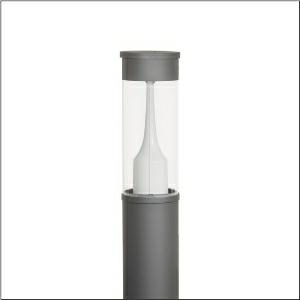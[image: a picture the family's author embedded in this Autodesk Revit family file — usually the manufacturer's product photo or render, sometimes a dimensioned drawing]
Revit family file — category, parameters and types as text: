
# Revit family: city-light_260_iq___st1_2a_5xa5295mf14h_84f0
name_source: partatom
category: Lighting Fixtures
units: mm (PartAtom-declared; Revit-internal decimal feet)

## family parameters
Cut with Voids When Loaded = No
Host = Face
Light Source = No
Part Type = Normal
Room Calculation Point = No
Round Connector Dimension = Use Diameter
Shared = No

## types (1)
- --- (1 x LED, 1540 lm, 11.8 W, 2700K)
    Apparent Load = 12 VA
    CIE Flux Codes = 22 61 93 96 100
    Color Rendering = 70
    Color Temperature = 2700K
    Default Elevation = 1800 mm
    Description = City-Light 260 iQ, light pillar, Module 540 iQ-SR, primary light control with 3 zone facetted reflector, of plastic, silver coated, highly specular, structured, primary optical cover: cover, of PMMA, transparent, partly coated, light distribution: ST1.2a, primary light characteristic: asymmetric, LED, High Power LED, rated luminous flux: 1.540lm, luminous efficacy: 131lm/W, light colour: 727, colour temperature: 2700K, control gear: ECG iQ, control: presetting dimming logarithmic, Street-Remote, Auto-Match, Temp-Guard, Lumen-Switch, Night-Set, Smart-Wire, Light-Fading, Desk-Remote (wireless, voltage-free reading and setting of iQ features in the workshop via application-optimized NFC function/RFID function), optimised constant luminous flux control (CLO 2.0), with terminal, 6-pole, max. 2.5mm², mains connection: 220..240V, AC, 50/60Hz, start of lifetime: 12W, end of lifetime: 12W, reduction: 6W, luminaire housing, cylindrical, of extruded aluminium section, coated, Siteco® metallic grey (DB 702S), length: 2.600mm, diameter: 200mm, Module 540 iQ-SR, traffic white (RAL 9016), equipment: standard, protection rating (complete): IP65, insulation class (complete): insulation class II (safety insulation), certification: CE, ENEC, VDE, packaging unit: 1 piece

Light Distribution: ST1.2a
    Height = 500 mm
    Lamp = 1 x LED
    Lamp Light Flux = 1540 lm
    Lamp Power = 11.8 W
    Lamp count = 1
    Length = 200 mm  [stored 0.656168 ft]
    Luminous efficacy = 131 lm/W
    Manufacturer = Siteco
    ModVariant = No
    Model = 5XA5295MF14H
    Number of Poles = 1
    OnlyDefault = Yes
    Power Factor = 1
    Product Name = City-Light 260 iQ | ST1.2a
    Product group = light pillar | pylon top
    ProductGroupID = 6103
    Protection Class = Protection class II
    Protection Degree = IP 65
    RLX_Detail_Level = 1
    RlxData = <blob elided: 60977 chars, md5=8d783912>
    Socket = socket
    Standby Power = 0 W
    System Light Flux = 1540 lm
    System Power = 12 W
    Type Comments = factory setting: luminous flux: 100 % | dim-lin: 254 | 472 mA
    Type Image = l_1006918.jpg
    URL = http://relux.com
    VarID = @adj_062929
    Voltage = 0 V
    Weight = 0.00 kg
    Width = 0 mm  [stored 0 ft]

note: [stored X ft] marks values corroborated as IEEE doubles in the binary element streams (Revit-internal decimal feet)

## geometry (parser evidence)
native form markers: Blend x4, Sweep x9
no freeform markers — native parametric forms only
